annotation { "Feature Type Name" : "Feature", "Feature Type Description" : "" }
export const myFeature = defineFeature(function(context is Context, id is Id, definition is map)
    precondition{}
    {
        {
            var Q0;
            Q0=qCreatedBy(makeId("Top.planeOp"),FACE);
            var sketch = newSketch(context, id + "F0", { "sketchPlane" : qUnion([Q0])});
            skLineSegment(sketch, "E0.bottom", {"start": v(38, -38) * mm, "end": v(-38, -38) * mm});
            skLineSegment(sketch, "E0.top", {"start": v(38, 38) * mm, "end": v(-38, 38) * mm});
            skLineSegment(sketch, "E0.left", {"start": v(38, -38) * mm, "end": v(38, 38) * mm});
            skLineSegment(sketch, "E0.right", {"start": v(-38, -38) * mm, "end": v(-38, 38) * mm});
            skPoint(sketch, "E0.middle", {"position": v(0, 0) * mm});
            skLineSegment(sketch, "E1.0", {"start": v(-35, -35) * mm, "end": v(-35, 35) * mm});
            skLineSegment(sketch, "E1.1", {"start": v(35, -35) * mm, "end": v(-35, -35) * mm});
            skLineSegment(sketch, "E1.2", {"start": v(35, -35) * mm, "end": v(35, 35) * mm});
            skLineSegment(sketch, "E1.3", {"start": v(35, 35) * mm, "end": v(-35, 35) * mm});
            skSolve(sketch);
        }
        {
            var Q0;
            Q0=makeQuery(id+"F0.imprint","IMPRINT",FACE,{"disambiguationData":[TD([[makeQuery(id+"F0.imprint","IMPRINT",EDGE,{"derivedFrom":sQuery(id+"F0.wireOp",EDGE,"E0.bottom")}),-1.0]])]});
            extrude(context, id + "F1", {"entities" : qUnion([Q0]), "depth" : 122 * mm, "offsetDistance" : 25 * mm});
        }
        {
            var Q0;
            Q0=makeQuery(id+"F0.imprint","IMPRINT",FACE,{"disambiguationData":[TD([[makeQuery(id+"F0.imprint","IMPRINT",EDGE,{"derivedFrom":sQuery(id+"F0.wireOp",EDGE,"E0.bottom")}),-1.0]])]});
            var Q1;
            Q1=makeQuery(id+"F0.imprint","IMPRINT",FACE,{"disambiguationData":[TD([[makeQuery(id+"F0.imprint","IMPRINT",EDGE,{"derivedFrom":sQuery(id+"F0.wireOp",EDGE,"E1.0")}),-1.0]])]});
            extrude(context, id + "F2", {"entities" : qUnion([Q0, Q1]), "operationType" : NewBodyOperationType.ADD, "oppositeDirection" : true, "depth" : 3 * mm, "offsetDistance" : 25 * mm});
        }
        {
            var Q0;
            {var subQ0=sQuery(id+"F0.wireOp",EDGE,"E0.top");Q0=makeQuery(id+"F2.boolean.opBoolean","MERGE",FACE,{"derivedFrom":[makeQuery(id+"F1.opExtrude","SWEPT_FACE",FACE,{"disambiguationData":[OSD([subQ0])]}),makeQuery(id+"F2.opExtrude","SWEPT_FACE",FACE,{"disambiguationData":[OSD([subQ0])]})]});}
            var sketch = newSketch(context, id + "F3", { "sketchPlane" : qUnion([Q0])});
            skCircle(sketch, "E2", {"center": v(-23.93, 112.63) * mm, "radius": 5.45 * mm});
            skCircle(sketch, "E3", {"center": v(-14.07, 99.88) * mm, "radius": 7.74 * mm});
            skCircle(sketch, "E4", {"center": v(-18.4, 76.32) * mm, "radius": 12.07 * mm});
            skCircle(sketch, "E5", {"center": v(8.3, 72.71) * mm, "radius": 9.52 * mm});
            skCircle(sketch, "E6", {"center": v(12.62, 91.47) * mm, "radius": 4.62 * mm});
            skCircle(sketch, "E7", {"center": v(0, 45.06) * mm, "radius": 3.83 * mm});
            skCircle(sketch, "E8", {"center": v(-13.35, 35.44) * mm, "radius": 5.61 * mm});
            skCircle(sketch, "E9", {"center": v(7.1, 18.6) * mm, "radius": 4.64 * mm});
            skCircle(sketch, "E10", {"center": v(17.43, 39.05) * mm, "radius": 6.47 * mm});
            skCircle(sketch, "E11", {"center": v(26.57, 57.56) * mm, "radius": 7.49 * mm});
            skCircle(sketch, "E12", {"center": v(8.78, 110.95) * mm, "radius": 4.28 * mm});
            skCircle(sketch, "E13", {"center": v(23.2, 107.1) * mm, "radius": 5.3 * mm});
            skCircle(sketch, "E14", {"center": v(-19.36, 53.71) * mm, "radius": 8 * mm});
            skCircle(sketch, "E15", {"center": v(-20.56, 18.85) * mm, "radius": 4.47 * mm});
            skCircle(sketch, "E16", {"center": v(-8.78, 9.23) * mm, "radius": 6.54 * mm});
            skCircle(sketch, "E17", {"center": v(22.96, 16.68) * mm, "radius": 3.91 * mm});
            skCircle(sketch, "E18", {"center": v(26.57, 7.06) * mm, "radius": 2.56 * mm});
            skCircle(sketch, "E19", {"center": v(9.74, 7.79) * mm, "radius": 3.68 * mm});
            skCircle(sketch, "E20", {"center": v(-28.98, 8.75) * mm, "radius": 4.34 * mm});
            skSolve(sketch);
        }
        {
            var Q0;
            Q0 = qSketchRegion(id + "F3", true);
            extrude(context, id + "F4", {"entities" : qUnion([Q0]), "oppositeDirection" : true, "depth" : 5 * mm, "offsetDistance" : 25 * mm});
        }
        {
            var Q0;
            Q0=qCreatedBy(makeId("Front.planeOp"),FACE);
            var sketch = newSketch(context, id + "F5", { "sketchPlane" : qUnion([Q0])});
            skLineSegment(sketch, "E21", {"start": v(0, 24.74) * mm, "end": v(0, 105.67) * mm, "construction": true});
            skSolve(sketch);
        }
        {
            var Q0;
            Q0=makeQuery(id+"F4.opExtrude","SWEPT_BODY",BODY,{"disambiguationData":[OSD([sQuery(id+"F3.wireOp",EDGE,"E2")])]});
            var Q1;
            Q1=makeQuery(id+"F4.opExtrude","SWEPT_BODY",BODY,{"disambiguationData":[OSD([sQuery(id+"F3.wireOp",EDGE,"E3")])]});
            var Q2;
            Q2=makeQuery(id+"F4.opExtrude","SWEPT_BODY",BODY,{"disambiguationData":[OSD([sQuery(id+"F3.wireOp",EDGE,"E4")])]});
            var Q3;
            Q3=makeQuery(id+"F4.opExtrude","SWEPT_BODY",BODY,{"disambiguationData":[OSD([sQuery(id+"F3.wireOp",EDGE,"E5")])]});
            var Q4;
            Q4=makeQuery(id+"F4.opExtrude","SWEPT_BODY",BODY,{"disambiguationData":[OSD([sQuery(id+"F3.wireOp",EDGE,"E6")])]});
            var Q5;
            Q5=makeQuery(id+"F4.opExtrude","SWEPT_BODY",BODY,{"disambiguationData":[OSD([sQuery(id+"F3.wireOp",EDGE,"E7")])]});
            var Q6;
            Q6=makeQuery(id+"F4.opExtrude","SWEPT_BODY",BODY,{"disambiguationData":[OSD([sQuery(id+"F3.wireOp",EDGE,"E8")])]});
            var Q7;
            Q7=makeQuery(id+"F4.opExtrude","SWEPT_BODY",BODY,{"disambiguationData":[OSD([sQuery(id+"F3.wireOp",EDGE,"E9")])]});
            var Q8;
            Q8=makeQuery(id+"F4.opExtrude","SWEPT_BODY",BODY,{"disambiguationData":[OSD([sQuery(id+"F3.wireOp",EDGE,"E10")])]});
            var Q9;
            Q9=makeQuery(id+"F4.opExtrude","SWEPT_BODY",BODY,{"disambiguationData":[OSD([sQuery(id+"F3.wireOp",EDGE,"E11")])]});
            var Q10;
            Q10=makeQuery(id+"F4.opExtrude","SWEPT_BODY",BODY,{"disambiguationData":[OSD([sQuery(id+"F3.wireOp",EDGE,"E12")])]});
            var Q11;
            Q11=makeQuery(id+"F4.opExtrude","SWEPT_BODY",BODY,{"disambiguationData":[OSD([sQuery(id+"F3.wireOp",EDGE,"E13")])]});
            var Q12;
            Q12=makeQuery(id+"F4.opExtrude","SWEPT_BODY",BODY,{"disambiguationData":[OSD([sQuery(id+"F3.wireOp",EDGE,"E14")])]});
            var Q13;
            Q13=makeQuery(id+"F4.opExtrude","SWEPT_BODY",BODY,{"disambiguationData":[OSD([sQuery(id+"F3.wireOp",EDGE,"E15")])]});
            var Q14;
            Q14=makeQuery(id+"F4.opExtrude","SWEPT_BODY",BODY,{"disambiguationData":[OSD([sQuery(id+"F3.wireOp",EDGE,"E16")])]});
            var Q15;
            Q15=makeQuery(id+"F4.opExtrude","SWEPT_BODY",BODY,{"disambiguationData":[OSD([sQuery(id+"F3.wireOp",EDGE,"E17")])]});
            var Q16;
            Q16=makeQuery(id+"F4.opExtrude","SWEPT_BODY",BODY,{"disambiguationData":[OSD([sQuery(id+"F3.wireOp",EDGE,"E18")])]});
            var Q17;
            Q17=makeQuery(id+"F4.opExtrude","SWEPT_BODY",BODY,{"disambiguationData":[OSD([sQuery(id+"F3.wireOp",EDGE,"E19")])]});
            var Q18;
            Q18=makeQuery(id+"F4.opExtrude","SWEPT_BODY",BODY,{"disambiguationData":[OSD([sQuery(id+"F3.wireOp",EDGE,"E20")])]});
            var Q19;
            Q19=sQuery(id+"F5.wireOp",EDGE,"E21");
            circularPattern(context, id + "F6", {"entities" : qUnion([Q0, Q1, Q2, Q3, Q4, Q5, Q6, Q7, Q8, Q9, Q10, Q11, Q12, Q13, Q14, Q15, Q16, Q17, Q18]), "axis" : qUnion([Q19]), "angle" : 360 * degree, "instanceCount" : 4, "equalSpace" : true});
        }
        {
            var Q0;
            Q0=makeQuery(id+"F4.opExtrude","SWEPT_BODY",BODY,{"disambiguationData":[OSD([sQuery(id+"F3.wireOp",EDGE,"E2")])]});
            var Q1;
            Q1=makeQuery(id+"F4.opExtrude","SWEPT_BODY",BODY,{"disambiguationData":[OSD([sQuery(id+"F3.wireOp",EDGE,"E3")])]});
            var Q2;
            Q2=makeQuery(id+"F4.opExtrude","SWEPT_BODY",BODY,{"disambiguationData":[OSD([sQuery(id+"F3.wireOp",EDGE,"E4")])]});
            var Q3;
            Q3=makeQuery(id+"F4.opExtrude","SWEPT_BODY",BODY,{"disambiguationData":[OSD([sQuery(id+"F3.wireOp",EDGE,"E5")])]});
            var Q4;
            Q4=makeQuery(id+"F4.opExtrude","SWEPT_BODY",BODY,{"disambiguationData":[OSD([sQuery(id+"F3.wireOp",EDGE,"E6")])]});
            var Q5;
            Q5=makeQuery(id+"F4.opExtrude","SWEPT_BODY",BODY,{"disambiguationData":[OSD([sQuery(id+"F3.wireOp",EDGE,"E7")])]});
            var Q6;
            Q6=makeQuery(id+"F4.opExtrude","SWEPT_BODY",BODY,{"disambiguationData":[OSD([sQuery(id+"F3.wireOp",EDGE,"E8")])]});
            var Q7;
            Q7=makeQuery(id+"F4.opExtrude","SWEPT_BODY",BODY,{"disambiguationData":[OSD([sQuery(id+"F3.wireOp",EDGE,"E9")])]});
            var Q8;
            Q8=makeQuery(id+"F4.opExtrude","SWEPT_BODY",BODY,{"disambiguationData":[OSD([sQuery(id+"F3.wireOp",EDGE,"E10")])]});
            var Q9;
            Q9=makeQuery(id+"F4.opExtrude","SWEPT_BODY",BODY,{"disambiguationData":[OSD([sQuery(id+"F3.wireOp",EDGE,"E11")])]});
            var Q10;
            Q10=makeQuery(id+"F4.opExtrude","SWEPT_BODY",BODY,{"disambiguationData":[OSD([sQuery(id+"F3.wireOp",EDGE,"E12")])]});
            var Q11;
            Q11=makeQuery(id+"F4.opExtrude","SWEPT_BODY",BODY,{"disambiguationData":[OSD([sQuery(id+"F3.wireOp",EDGE,"E13")])]});
            var Q12;
            Q12=makeQuery(id+"F4.opExtrude","SWEPT_BODY",BODY,{"disambiguationData":[OSD([sQuery(id+"F3.wireOp",EDGE,"E14")])]});
            var Q13;
            Q13=makeQuery(id+"F4.opExtrude","SWEPT_BODY",BODY,{"disambiguationData":[OSD([sQuery(id+"F3.wireOp",EDGE,"E15")])]});
            var Q14;
            Q14=makeQuery(id+"F4.opExtrude","SWEPT_BODY",BODY,{"disambiguationData":[OSD([sQuery(id+"F3.wireOp",EDGE,"E16")])]});
            var Q15;
            Q15=makeQuery(id+"F4.opExtrude","SWEPT_BODY",BODY,{"disambiguationData":[OSD([sQuery(id+"F3.wireOp",EDGE,"E17")])]});
            var Q16;
            Q16=makeQuery(id+"F4.opExtrude","SWEPT_BODY",BODY,{"disambiguationData":[OSD([sQuery(id+"F3.wireOp",EDGE,"E18")])]});
            var Q17;
            Q17=makeQuery(id+"F4.opExtrude","SWEPT_BODY",BODY,{"disambiguationData":[OSD([sQuery(id+"F3.wireOp",EDGE,"E19")])]});
            var Q18;
            Q18=makeQuery(id+"F4.opExtrude","SWEPT_BODY",BODY,{"disambiguationData":[OSD([sQuery(id+"F3.wireOp",EDGE,"E20")])]});
            var Q19;
            Q19=makeQuery(id+"F6.opPattern","COPY",BODY,{"derivedFrom":makeQuery(id+"F4.opExtrude","SWEPT_BODY",BODY,{"disambiguationData":[OSD([sQuery(id+"F3.wireOp",EDGE,"E2")])]}),"instanceName":"1"});
            var Q20;
            Q20=makeQuery(id+"F6.opPattern","COPY",BODY,{"derivedFrom":makeQuery(id+"F4.opExtrude","SWEPT_BODY",BODY,{"disambiguationData":[OSD([sQuery(id+"F3.wireOp",EDGE,"E3")])]}),"instanceName":"1"});
            var Q21;
            Q21=makeQuery(id+"F6.opPattern","COPY",BODY,{"derivedFrom":makeQuery(id+"F4.opExtrude","SWEPT_BODY",BODY,{"disambiguationData":[OSD([sQuery(id+"F3.wireOp",EDGE,"E4")])]}),"instanceName":"1"});
            var Q22;
            Q22=makeQuery(id+"F6.opPattern","COPY",BODY,{"derivedFrom":makeQuery(id+"F4.opExtrude","SWEPT_BODY",BODY,{"disambiguationData":[OSD([sQuery(id+"F3.wireOp",EDGE,"E5")])]}),"instanceName":"1"});
            var Q23;
            Q23=makeQuery(id+"F6.opPattern","COPY",BODY,{"derivedFrom":makeQuery(id+"F4.opExtrude","SWEPT_BODY",BODY,{"disambiguationData":[OSD([sQuery(id+"F3.wireOp",EDGE,"E6")])]}),"instanceName":"1"});
            var Q24;
            Q24=makeQuery(id+"F6.opPattern","COPY",BODY,{"derivedFrom":makeQuery(id+"F4.opExtrude","SWEPT_BODY",BODY,{"disambiguationData":[OSD([sQuery(id+"F3.wireOp",EDGE,"E7")])]}),"instanceName":"1"});
            var Q25;
            Q25=makeQuery(id+"F6.opPattern","COPY",BODY,{"derivedFrom":makeQuery(id+"F4.opExtrude","SWEPT_BODY",BODY,{"disambiguationData":[OSD([sQuery(id+"F3.wireOp",EDGE,"E8")])]}),"instanceName":"1"});
            var Q26;
            Q26=makeQuery(id+"F6.opPattern","COPY",BODY,{"derivedFrom":makeQuery(id+"F4.opExtrude","SWEPT_BODY",BODY,{"disambiguationData":[OSD([sQuery(id+"F3.wireOp",EDGE,"E9")])]}),"instanceName":"1"});
            var Q27;
            Q27=makeQuery(id+"F6.opPattern","COPY",BODY,{"derivedFrom":makeQuery(id+"F4.opExtrude","SWEPT_BODY",BODY,{"disambiguationData":[OSD([sQuery(id+"F3.wireOp",EDGE,"E10")])]}),"instanceName":"1"});
            var Q28;
            Q28=makeQuery(id+"F6.opPattern","COPY",BODY,{"derivedFrom":makeQuery(id+"F4.opExtrude","SWEPT_BODY",BODY,{"disambiguationData":[OSD([sQuery(id+"F3.wireOp",EDGE,"E11")])]}),"instanceName":"1"});
            var Q29;
            Q29=makeQuery(id+"F6.opPattern","COPY",BODY,{"derivedFrom":makeQuery(id+"F4.opExtrude","SWEPT_BODY",BODY,{"disambiguationData":[OSD([sQuery(id+"F3.wireOp",EDGE,"E12")])]}),"instanceName":"1"});
            var Q30;
            Q30=makeQuery(id+"F6.opPattern","COPY",BODY,{"derivedFrom":makeQuery(id+"F4.opExtrude","SWEPT_BODY",BODY,{"disambiguationData":[OSD([sQuery(id+"F3.wireOp",EDGE,"E13")])]}),"instanceName":"1"});
            var Q31;
            Q31=makeQuery(id+"F6.opPattern","COPY",BODY,{"derivedFrom":makeQuery(id+"F4.opExtrude","SWEPT_BODY",BODY,{"disambiguationData":[OSD([sQuery(id+"F3.wireOp",EDGE,"E14")])]}),"instanceName":"1"});
            var Q32;
            Q32=makeQuery(id+"F6.opPattern","COPY",BODY,{"derivedFrom":makeQuery(id+"F4.opExtrude","SWEPT_BODY",BODY,{"disambiguationData":[OSD([sQuery(id+"F3.wireOp",EDGE,"E15")])]}),"instanceName":"1"});
            var Q33;
            Q33=makeQuery(id+"F6.opPattern","COPY",BODY,{"derivedFrom":makeQuery(id+"F4.opExtrude","SWEPT_BODY",BODY,{"disambiguationData":[OSD([sQuery(id+"F3.wireOp",EDGE,"E16")])]}),"instanceName":"1"});
            var Q34;
            Q34=makeQuery(id+"F6.opPattern","COPY",BODY,{"derivedFrom":makeQuery(id+"F4.opExtrude","SWEPT_BODY",BODY,{"disambiguationData":[OSD([sQuery(id+"F3.wireOp",EDGE,"E17")])]}),"instanceName":"1"});
            var Q35;
            Q35=makeQuery(id+"F6.opPattern","COPY",BODY,{"derivedFrom":makeQuery(id+"F4.opExtrude","SWEPT_BODY",BODY,{"disambiguationData":[OSD([sQuery(id+"F3.wireOp",EDGE,"E18")])]}),"instanceName":"1"});
            var Q36;
            Q36=makeQuery(id+"F6.opPattern","COPY",BODY,{"derivedFrom":makeQuery(id+"F4.opExtrude","SWEPT_BODY",BODY,{"disambiguationData":[OSD([sQuery(id+"F3.wireOp",EDGE,"E19")])]}),"instanceName":"1"});
            var Q37;
            Q37=makeQuery(id+"F6.opPattern","COPY",BODY,{"derivedFrom":makeQuery(id+"F4.opExtrude","SWEPT_BODY",BODY,{"disambiguationData":[OSD([sQuery(id+"F3.wireOp",EDGE,"E20")])]}),"instanceName":"1"});
            var Q38;
            Q38=makeQuery(id+"F6.opPattern","COPY",BODY,{"derivedFrom":makeQuery(id+"F4.opExtrude","SWEPT_BODY",BODY,{"disambiguationData":[OSD([sQuery(id+"F3.wireOp",EDGE,"E2")])]}),"instanceName":"2"});
            var Q39;
            Q39=makeQuery(id+"F6.opPattern","COPY",BODY,{"derivedFrom":makeQuery(id+"F4.opExtrude","SWEPT_BODY",BODY,{"disambiguationData":[OSD([sQuery(id+"F3.wireOp",EDGE,"E3")])]}),"instanceName":"2"});
            var Q40;
            Q40=makeQuery(id+"F6.opPattern","COPY",BODY,{"derivedFrom":makeQuery(id+"F4.opExtrude","SWEPT_BODY",BODY,{"disambiguationData":[OSD([sQuery(id+"F3.wireOp",EDGE,"E4")])]}),"instanceName":"2"});
            var Q41;
            Q41=makeQuery(id+"F6.opPattern","COPY",BODY,{"derivedFrom":makeQuery(id+"F4.opExtrude","SWEPT_BODY",BODY,{"disambiguationData":[OSD([sQuery(id+"F3.wireOp",EDGE,"E5")])]}),"instanceName":"2"});
            var Q42;
            Q42=makeQuery(id+"F6.opPattern","COPY",BODY,{"derivedFrom":makeQuery(id+"F4.opExtrude","SWEPT_BODY",BODY,{"disambiguationData":[OSD([sQuery(id+"F3.wireOp",EDGE,"E6")])]}),"instanceName":"2"});
            var Q43;
            Q43=makeQuery(id+"F6.opPattern","COPY",BODY,{"derivedFrom":makeQuery(id+"F4.opExtrude","SWEPT_BODY",BODY,{"disambiguationData":[OSD([sQuery(id+"F3.wireOp",EDGE,"E7")])]}),"instanceName":"2"});
            var Q44;
            Q44=makeQuery(id+"F6.opPattern","COPY",BODY,{"derivedFrom":makeQuery(id+"F4.opExtrude","SWEPT_BODY",BODY,{"disambiguationData":[OSD([sQuery(id+"F3.wireOp",EDGE,"E8")])]}),"instanceName":"2"});
            var Q45;
            Q45=makeQuery(id+"F6.opPattern","COPY",BODY,{"derivedFrom":makeQuery(id+"F4.opExtrude","SWEPT_BODY",BODY,{"disambiguationData":[OSD([sQuery(id+"F3.wireOp",EDGE,"E9")])]}),"instanceName":"2"});
            var Q46;
            Q46=makeQuery(id+"F6.opPattern","COPY",BODY,{"derivedFrom":makeQuery(id+"F4.opExtrude","SWEPT_BODY",BODY,{"disambiguationData":[OSD([sQuery(id+"F3.wireOp",EDGE,"E10")])]}),"instanceName":"2"});
            var Q47;
            Q47=makeQuery(id+"F6.opPattern","COPY",BODY,{"derivedFrom":makeQuery(id+"F4.opExtrude","SWEPT_BODY",BODY,{"disambiguationData":[OSD([sQuery(id+"F3.wireOp",EDGE,"E11")])]}),"instanceName":"2"});
            var Q48;
            Q48=makeQuery(id+"F6.opPattern","COPY",BODY,{"derivedFrom":makeQuery(id+"F4.opExtrude","SWEPT_BODY",BODY,{"disambiguationData":[OSD([sQuery(id+"F3.wireOp",EDGE,"E12")])]}),"instanceName":"2"});
            var Q49;
            Q49=makeQuery(id+"F6.opPattern","COPY",BODY,{"derivedFrom":makeQuery(id+"F4.opExtrude","SWEPT_BODY",BODY,{"disambiguationData":[OSD([sQuery(id+"F3.wireOp",EDGE,"E13")])]}),"instanceName":"2"});
            var Q50;
            Q50=makeQuery(id+"F6.opPattern","COPY",BODY,{"derivedFrom":makeQuery(id+"F4.opExtrude","SWEPT_BODY",BODY,{"disambiguationData":[OSD([sQuery(id+"F3.wireOp",EDGE,"E14")])]}),"instanceName":"2"});
            var Q51;
            Q51=makeQuery(id+"F6.opPattern","COPY",BODY,{"derivedFrom":makeQuery(id+"F4.opExtrude","SWEPT_BODY",BODY,{"disambiguationData":[OSD([sQuery(id+"F3.wireOp",EDGE,"E15")])]}),"instanceName":"2"});
            var Q52;
            Q52=makeQuery(id+"F6.opPattern","COPY",BODY,{"derivedFrom":makeQuery(id+"F4.opExtrude","SWEPT_BODY",BODY,{"disambiguationData":[OSD([sQuery(id+"F3.wireOp",EDGE,"E16")])]}),"instanceName":"2"});
            var Q53;
            Q53=makeQuery(id+"F6.opPattern","COPY",BODY,{"derivedFrom":makeQuery(id+"F4.opExtrude","SWEPT_BODY",BODY,{"disambiguationData":[OSD([sQuery(id+"F3.wireOp",EDGE,"E17")])]}),"instanceName":"2"});
            var Q54;
            Q54=makeQuery(id+"F6.opPattern","COPY",BODY,{"derivedFrom":makeQuery(id+"F4.opExtrude","SWEPT_BODY",BODY,{"disambiguationData":[OSD([sQuery(id+"F3.wireOp",EDGE,"E18")])]}),"instanceName":"2"});
            var Q55;
            Q55=makeQuery(id+"F6.opPattern","COPY",BODY,{"derivedFrom":makeQuery(id+"F4.opExtrude","SWEPT_BODY",BODY,{"disambiguationData":[OSD([sQuery(id+"F3.wireOp",EDGE,"E19")])]}),"instanceName":"2"});
            var Q56;
            Q56=makeQuery(id+"F6.opPattern","COPY",BODY,{"derivedFrom":makeQuery(id+"F4.opExtrude","SWEPT_BODY",BODY,{"disambiguationData":[OSD([sQuery(id+"F3.wireOp",EDGE,"E20")])]}),"instanceName":"2"});
            var Q57;
            Q57=makeQuery(id+"F6.opPattern","COPY",BODY,{"derivedFrom":makeQuery(id+"F4.opExtrude","SWEPT_BODY",BODY,{"disambiguationData":[OSD([sQuery(id+"F3.wireOp",EDGE,"E2")])]}),"instanceName":"3"});
            var Q58;
            Q58=makeQuery(id+"F6.opPattern","COPY",BODY,{"derivedFrom":makeQuery(id+"F4.opExtrude","SWEPT_BODY",BODY,{"disambiguationData":[OSD([sQuery(id+"F3.wireOp",EDGE,"E3")])]}),"instanceName":"3"});
            var Q59;
            Q59=makeQuery(id+"F6.opPattern","COPY",BODY,{"derivedFrom":makeQuery(id+"F4.opExtrude","SWEPT_BODY",BODY,{"disambiguationData":[OSD([sQuery(id+"F3.wireOp",EDGE,"E4")])]}),"instanceName":"3"});
            var Q60;
            Q60=makeQuery(id+"F6.opPattern","COPY",BODY,{"derivedFrom":makeQuery(id+"F4.opExtrude","SWEPT_BODY",BODY,{"disambiguationData":[OSD([sQuery(id+"F3.wireOp",EDGE,"E5")])]}),"instanceName":"3"});
            var Q61;
            Q61=makeQuery(id+"F6.opPattern","COPY",BODY,{"derivedFrom":makeQuery(id+"F4.opExtrude","SWEPT_BODY",BODY,{"disambiguationData":[OSD([sQuery(id+"F3.wireOp",EDGE,"E6")])]}),"instanceName":"3"});
            var Q62;
            Q62=makeQuery(id+"F6.opPattern","COPY",BODY,{"derivedFrom":makeQuery(id+"F4.opExtrude","SWEPT_BODY",BODY,{"disambiguationData":[OSD([sQuery(id+"F3.wireOp",EDGE,"E7")])]}),"instanceName":"3"});
            var Q63;
            Q63=makeQuery(id+"F6.opPattern","COPY",BODY,{"derivedFrom":makeQuery(id+"F4.opExtrude","SWEPT_BODY",BODY,{"disambiguationData":[OSD([sQuery(id+"F3.wireOp",EDGE,"E8")])]}),"instanceName":"3"});
            var Q64;
            Q64=makeQuery(id+"F6.opPattern","COPY",BODY,{"derivedFrom":makeQuery(id+"F4.opExtrude","SWEPT_BODY",BODY,{"disambiguationData":[OSD([sQuery(id+"F3.wireOp",EDGE,"E9")])]}),"instanceName":"3"});
            var Q65;
            Q65=makeQuery(id+"F6.opPattern","COPY",BODY,{"derivedFrom":makeQuery(id+"F4.opExtrude","SWEPT_BODY",BODY,{"disambiguationData":[OSD([sQuery(id+"F3.wireOp",EDGE,"E10")])]}),"instanceName":"3"});
            var Q66;
            Q66=makeQuery(id+"F6.opPattern","COPY",BODY,{"derivedFrom":makeQuery(id+"F4.opExtrude","SWEPT_BODY",BODY,{"disambiguationData":[OSD([sQuery(id+"F3.wireOp",EDGE,"E11")])]}),"instanceName":"3"});
            var Q67;
            Q67=makeQuery(id+"F6.opPattern","COPY",BODY,{"derivedFrom":makeQuery(id+"F4.opExtrude","SWEPT_BODY",BODY,{"disambiguationData":[OSD([sQuery(id+"F3.wireOp",EDGE,"E12")])]}),"instanceName":"3"});
            var Q68;
            Q68=makeQuery(id+"F6.opPattern","COPY",BODY,{"derivedFrom":makeQuery(id+"F4.opExtrude","SWEPT_BODY",BODY,{"disambiguationData":[OSD([sQuery(id+"F3.wireOp",EDGE,"E13")])]}),"instanceName":"3"});
            var Q69;
            Q69=makeQuery(id+"F6.opPattern","COPY",BODY,{"derivedFrom":makeQuery(id+"F4.opExtrude","SWEPT_BODY",BODY,{"disambiguationData":[OSD([sQuery(id+"F3.wireOp",EDGE,"E14")])]}),"instanceName":"3"});
            var Q70;
            Q70=makeQuery(id+"F6.opPattern","COPY",BODY,{"derivedFrom":makeQuery(id+"F4.opExtrude","SWEPT_BODY",BODY,{"disambiguationData":[OSD([sQuery(id+"F3.wireOp",EDGE,"E15")])]}),"instanceName":"3"});
            var Q71;
            Q71=makeQuery(id+"F6.opPattern","COPY",BODY,{"derivedFrom":makeQuery(id+"F4.opExtrude","SWEPT_BODY",BODY,{"disambiguationData":[OSD([sQuery(id+"F3.wireOp",EDGE,"E16")])]}),"instanceName":"3"});
            var Q72;
            Q72=makeQuery(id+"F6.opPattern","COPY",BODY,{"derivedFrom":makeQuery(id+"F4.opExtrude","SWEPT_BODY",BODY,{"disambiguationData":[OSD([sQuery(id+"F3.wireOp",EDGE,"E17")])]}),"instanceName":"3"});
            var Q73;
            Q73=makeQuery(id+"F6.opPattern","COPY",BODY,{"derivedFrom":makeQuery(id+"F4.opExtrude","SWEPT_BODY",BODY,{"disambiguationData":[OSD([sQuery(id+"F3.wireOp",EDGE,"E18")])]}),"instanceName":"3"});
            var Q74;
            Q74=makeQuery(id+"F6.opPattern","COPY",BODY,{"derivedFrom":makeQuery(id+"F4.opExtrude","SWEPT_BODY",BODY,{"disambiguationData":[OSD([sQuery(id+"F3.wireOp",EDGE,"E19")])]}),"instanceName":"3"});
            var Q75;
            Q75=makeQuery(id+"F6.opPattern","COPY",BODY,{"derivedFrom":makeQuery(id+"F4.opExtrude","SWEPT_BODY",BODY,{"disambiguationData":[OSD([sQuery(id+"F3.wireOp",EDGE,"E20")])]}),"instanceName":"3"});
            var Q76;
            Q76=makeQuery(id+"F1.opExtrude","SWEPT_BODY",BODY,{"disambiguationData":[OSD([sQuery(id+"F0.wireOp",EDGE,"E0.bottom"),sQuery(id+"F0.wireOp",EDGE,"E0.top"),sQuery(id+"F0.wireOp",EDGE,"E0.left"),sQuery(id+"F0.wireOp",EDGE,"E0.right"),sQuery(id+"F0.wireOp",EDGE,"E1.0"),sQuery(id+"F0.wireOp",EDGE,"E1.1"),sQuery(id+"F0.wireOp",EDGE,"E1.2"),sQuery(id+"F0.wireOp",EDGE,"E1.3")])]});
            booleanBodies(context, id + "F7", {"operationType" : BooleanOperationType.SUBTRACTION, "tools" : qUnion([Q0, Q1, Q2, Q3, Q4, Q5, Q6, Q7, Q8, Q9, Q10, Q11, Q12, Q13, Q14, Q15, Q16, Q17, Q18, Q19, Q20, Q21, Q22, Q23, Q24, Q25, Q26, Q27, Q28, Q29, Q30, Q31, Q32, Q33, Q34, Q35, Q36, Q37, Q38, Q39, Q40, Q41, Q42, Q43, Q44, Q45, Q46, Q47, Q48, Q49, Q50, Q51, Q52, Q53, Q54, Q55, Q56, Q57, Q58, Q59, Q60, Q61, Q62, Q63, Q64, Q65, Q66, Q67, Q68, Q69, Q70, Q71, Q72, Q73, Q74, Q75]), "targets" : qUnion([Q76])});
        }
        {
            var Q0;
            {var subQ0=sQuery(id+"F0.wireOp",EDGE,"E0.left");var subQ1=sQuery(id+"F0.wireOp",EDGE,"E0.bottom");Q0=makeQuery(id+"F2.boolean.opBoolean","MERGE",EDGE,{"derivedFrom":[makeQuery(id+"F1.opExtrude","SWEPT_EDGE",EDGE,{"disambiguationData":[OSD([subQ1,subQ0])]}),makeQuery(id+"F2.opExtrude","SWEPT_EDGE",EDGE,{"disambiguationData":[OSD([subQ1,subQ0])]})]});}
            var Q1;
            {var subQ0=sQuery(id+"F0.wireOp",EDGE,"E0.left");var subQ1=sQuery(id+"F0.wireOp",EDGE,"E0.top");Q1=makeQuery(id+"F2.boolean.opBoolean","MERGE",EDGE,{"derivedFrom":[makeQuery(id+"F1.opExtrude","SWEPT_EDGE",EDGE,{"disambiguationData":[OSD([subQ1,subQ0])]}),makeQuery(id+"F2.opExtrude","SWEPT_EDGE",EDGE,{"disambiguationData":[OSD([subQ1,subQ0])]})]});}
            var Q2;
            {var subQ0=sQuery(id+"F0.wireOp",EDGE,"E0.right");var subQ1=sQuery(id+"F0.wireOp",EDGE,"E0.top");Q2=makeQuery(id+"F2.boolean.opBoolean","MERGE",EDGE,{"derivedFrom":[makeQuery(id+"F1.opExtrude","SWEPT_EDGE",EDGE,{"disambiguationData":[OSD([subQ1,subQ0])]}),makeQuery(id+"F2.opExtrude","SWEPT_EDGE",EDGE,{"disambiguationData":[OSD([subQ1,subQ0])]})]});}
            var Q3;
            {var subQ0=sQuery(id+"F0.wireOp",EDGE,"E0.right");var subQ1=sQuery(id+"F0.wireOp",EDGE,"E0.bottom");Q3=makeQuery(id+"F2.boolean.opBoolean","MERGE",EDGE,{"derivedFrom":[makeQuery(id+"F1.opExtrude","SWEPT_EDGE",EDGE,{"disambiguationData":[OSD([subQ1,subQ0])]}),makeQuery(id+"F2.opExtrude","SWEPT_EDGE",EDGE,{"disambiguationData":[OSD([subQ1,subQ0])]})]});}
            var Q4;
            Q4=makeQuery(id+"F1.opExtrude","SWEPT_EDGE",EDGE,{"disambiguationData":[OSD([sQuery(id+"F0.wireOp",EDGE,"E1.0"),sQuery(id+"F0.wireOp",EDGE,"E1.1")])]});
            var Q5;
            Q5=makeQuery(id+"F1.opExtrude","SWEPT_EDGE",EDGE,{"disambiguationData":[OSD([sQuery(id+"F0.wireOp",EDGE,"E1.1"),sQuery(id+"F0.wireOp",EDGE,"E1.2")])]});
            var Q6;
            Q6=makeQuery(id+"F1.opExtrude","SWEPT_EDGE",EDGE,{"disambiguationData":[OSD([sQuery(id+"F0.wireOp",EDGE,"E1.2"),sQuery(id+"F0.wireOp",EDGE,"E1.3")])]});
            var Q7;
            Q7=makeQuery(id+"F1.opExtrude","SWEPT_EDGE",EDGE,{"disambiguationData":[OSD([sQuery(id+"F0.wireOp",EDGE,"E1.0"),sQuery(id+"F0.wireOp",EDGE,"E1.3")])]});
            fillet(context, id + "F8", {"entities" : qUnion([Q0, Q1, Q2, Q3, Q4, Q5, Q6, Q7]), "radius" : 5 * mm, "tangentPropagation" : true, "allowEdgeOverflow" : false});
        }
        {
            var Q0;
            Q0=makeQuery(id+"F1.opExtrude","CAP_FACE",FACE,{"disambiguationData":[OSD([sQuery(id+"F0.wireOp",EDGE,"E0.bottom"),sQuery(id+"F0.wireOp",EDGE,"E0.top"),sQuery(id+"F0.wireOp",EDGE,"E0.left"),sQuery(id+"F0.wireOp",EDGE,"E0.right"),sQuery(id+"F0.wireOp",EDGE,"E1.0"),sQuery(id+"F0.wireOp",EDGE,"E1.1"),sQuery(id+"F0.wireOp",EDGE,"E1.2"),sQuery(id+"F0.wireOp",EDGE,"E1.3")])],"isStart":false});
            fillet(context, id + "F9", {"entities" : qUnion([Q0]), "radius" : 1 * mm, "tangentPropagation" : true, "allowEdgeOverflow" : false});
        }
        {
            var Q0;
            Q0=makeQuery(id+"F2.opExtrude","CAP_FACE",FACE,{"disambiguationData":[OSD([sQuery(id+"F0.wireOp",EDGE,"E0.bottom"),sQuery(id+"F0.wireOp",EDGE,"E0.top"),sQuery(id+"F0.wireOp",EDGE,"E0.left"),sQuery(id+"F0.wireOp",EDGE,"E0.right")])],"isStart":false});
            var sketch = newSketch(context, id + "F10", { "sketchPlane" : qUnion([Q0])});
            skText(sketch, "E22", { "text": "Chiang Mai", "fontName": "OpenSans-Bold.ttf"});
            skText(sketch, "E23", { "text": "Maker Club", "fontName": "OpenSans-Bold.ttf"});
            const initialGuessF10  = {"E22": [-0.033, -0.0006, 1, 0, 0.0086], "E23": [-0.03, -0.018, 1, 0, 0.00755]};
            skSetInitialGuess(sketch, initialGuessF10);
            skSolve(sketch);
        }
        {
            var Q0;
            Q0 = qSketchRegion(id + "F10", true);
            extrude(context, id + "F11", {"entities" : qUnion([Q0]), "operationType" : NewBodyOperationType.REMOVE, "oppositeDirection" : true, "depth" : 1 * mm, "offsetDistance" : 25 * mm});
        }
        {
            var Q0;
            {var subQ0=sQuery(id+"F0.wireOp",EDGE,"E0.right");var subQ1=sQuery(id+"F0.wireOp",EDGE,"E0.left");var subQ2=sQuery(id+"F0.wireOp",EDGE,"E0.top");var subQ3=sQuery(id+"F0.wireOp",EDGE,"E0.bottom");Q0=makeQuery(id+"F11.boolean.opBoolean","SPLIT",FACE,{"disambiguationData":[TD([makeQuery(id+"F1.opExtrude","SWEPT_FACE",FACE,{"disambiguationData":[OSD([subQ3])]})])],"derivedFrom":makeQuery(id+"F2.opExtrude","CAP_FACE",FACE,{"disambiguationData":[OSD([subQ3,subQ2,subQ1,subQ0])],"isStart":false})});}
            var sketch = newSketch(context, id + "F12", { "sketchPlane" : qUnion([Q0])});
            skLineSegment(sketch, "E24", {"start": v(-6.59, 21.1) * mm, "end": v(-6.59, 22.56) * mm});
            skLineSegment(sketch, "E25", {"start": v(-6.59, 22.56) * mm, "end": v(-4.62, 24.4) * mm});
            skLineSegment(sketch, "E26", {"start": v(-4.62, 24.4) * mm, "end": v(-2.03, 21.88) * mm});
            skLineSegment(sketch, "E27", {"start": v(-2.03, 21.88) * mm, "end": v(0.63, 24.4) * mm});
            skLineSegment(sketch, "E28", {"start": v(0.63, 24.4) * mm, "end": v(2.5, 22.63) * mm});
            skLineSegment(sketch, "E29", {"start": v(2.5, 22.63) * mm, "end": v(2.5, 21.06) * mm});
            skLineSegment(sketch, "E30", {"start": v(2.5, 21.06) * mm, "end": v(3.04, 21.06) * mm});
            skLineSegment(sketch, "E31", {"start": v(3.04, 21.06) * mm, "end": v(3.04, 22.96) * mm});
            skLineSegment(sketch, "E32", {"start": v(3.04, 22.96) * mm, "end": v(1.01, 24.9) * mm});
            skLineSegment(sketch, "E33", {"start": v(1.01, 24.9) * mm, "end": v(0.27, 24.9) * mm});
            skLineSegment(sketch, "E34", {"start": v(0.27, 24.9) * mm, "end": v(-1.96, 22.77) * mm});
            skLineSegment(sketch, "E35", {"start": v(-1.96, 22.77) * mm, "end": v(-4.3, 24.94) * mm});
            skLineSegment(sketch, "E36", {"start": v(-4.3, 24.94) * mm, "end": v(-5.03, 24.94) * mm});
            skLineSegment(sketch, "E37", {"start": v(-5.03, 24.94) * mm, "end": v(-7.17, 22.88) * mm});
            skLineSegment(sketch, "E38", {"start": v(-7.17, 22.88) * mm, "end": v(-7.17, 21.07) * mm});
            skLineSegment(sketch, "E39", {"start": v(-7.17, 21.07) * mm, "end": v(-6.59, 21.1) * mm});
            skLineSegment(sketch, "E40", {"start": v(-5.53, 24.74) * mm, "end": v(-4.98, 25.14) * mm});
            skFitSpline(sketch, "E41", {"points": [v(-4.98, 25.14) * mm, v(-4.88, 26.3) * mm, v(-4.52, 27.65) * mm, v(-3.66, 28.56) * mm, v(-2.66, 29.01) * mm, v(-1.23, 28.98) * mm, v(-0.11, 28.48) * mm, v(0.57, 27.63) * mm, v(0.93, 26.69) * mm, v(1.06, 25.9) * mm, v(1.07, 25.14) * mm], "startDerivative": vector(0.71, 11.03) * mm, "endDerivative": vector(-0.07, -9.21) * mm});
            skLineSegment(sketch, "E42", {"start": v(1.07, 25.14) * mm, "end": v(1.7, 24.62) * mm});
            skFitSpline(sketch, "E43", {"points": [v(1.7, 24.62) * mm, v(1.7, 25.54) * mm, v(1.5, 26.82) * mm, v(1, 28.05) * mm, v(0.2, 28.9) * mm, v(-0.9, 29.43) * mm, v(-2.04, 29.57) * mm, v(-3.08, 29.44) * mm, v(-3.98, 29.02) * mm, v(-4.64, 28.5) * mm, v(-5.21, 27.52) * mm, v(-5.5, 26.34) * mm, v(-5.58, 25.32) * mm, v(-5.53, 24.74) * mm], "startDerivative": vector(0.4, 12.35) * mm, "endDerivative": vector(2.9, -8.52) * mm});
            skLineSegment(sketch, "E44", {"start": v(-2.36, 29.56) * mm, "end": v(-2.36, 30.75) * mm});
            skLineSegment(sketch, "E45", {"start": v(-2.36, 30.75) * mm, "end": v(-2.07, 31.06) * mm});
            skLineSegment(sketch, "E46", {"start": v(-2.07, 31.06) * mm, "end": v(-1.74, 30.75) * mm});
            skLineSegment(sketch, "E47", {"start": v(-1.74, 30.75) * mm, "end": v(-1.74, 29.56) * mm});
            skLineSegment(sketch, "E48", {"start": v(0.94, 23.74) * mm, "end": v(1.42, 23.26) * mm});
            skFitSpline(sketch, "E49", {"points": [v(1.42, 23.26) * mm, v(1.36, 22.7) * mm, v(1.18, 21.88) * mm, v(0.88, 21.02) * mm, v(0.6, 20.4) * mm], "startDerivative": vector(-0.19, -2.45) * mm, "endDerivative": vector(-1.2, -2.47) * mm});
            skFitSpline(sketch, "E50", {"points": [v(0.94, 23.74) * mm, v(0.85, 23.13) * mm, v(0.68, 22.42) * mm, v(0.41, 21.59) * mm, v(0.1, 20.86) * mm, v(-0.18, 20.33) * mm, v(-0.38, 19.99) * mm, v(-0.62, 19.66) * mm, v(-0.95, 19.27) * mm, v(-1.27, 19.02) * mm, v(-1.46, 18.88) * mm, v(-2.26, 18.85) * mm, v(-2.8, 19.13) * mm, v(-3.08, 19.43) * mm, v(-3.6, 20.04) * mm, v(-3.86, 20.54) * mm, v(-4.12, 21.14) * mm, v(-4.31, 21.59) * mm, v(-4.48, 22.05) * mm, v(-4.6, 22.43) * mm, v(-4.73, 23.01) * mm, v(-4.8, 23.43) * mm, v(-4.9, 23.98) * mm], "startDerivative": vector(-1.52, -12.5) * mm, "endDerivative": vector(-2.96, 12.5) * mm});
            skLineSegment(sketch, "E51", {"start": v(-4.86, 23.79) * mm, "end": v(-5.43, 23.36) * mm});
            skFitSpline(sketch, "E52", {"points": [v(-5.43, 23.36) * mm, v(-5.36, 22.95) * mm, v(-5.25, 22.51) * mm, v(-5.14, 22.1) * mm, v(-5, 21.65) * mm, v(-4.9, 21.31) * mm, v(-4.78, 21.01) * mm, v(-4.65, 20.63) * mm, v(-4.51, 20.4) * mm, v(-4.5, 20.4) * mm], "startDerivative": vector(0.43, -3.16) * mm, "endDerivative": vector(0.3, 0.61) * mm});
            skLineSegment(sketch, "E53", {"start": v(-4.5, 20.4) * mm, "end": v(-6.33, 20.4) * mm});
            skLineSegment(sketch, "E54", {"start": v(-6.33, 20.4) * mm, "end": v(-6.6, 20.64) * mm});
            skLineSegment(sketch, "E55", {"start": v(-6.6, 20.64) * mm, "end": v(-7.12, 20.64) * mm});
            skLineSegment(sketch, "E56", {"start": v(-7.12, 20.64) * mm, "end": v(-7.12, 20.15) * mm});
            skFitSpline(sketch, "E57", {"points": [v(-7.12, 20.15) * mm, v(-6.85, 19.87) * mm, v(-6.53, 19.75) * mm], "startDerivative": vector(0.48, -0.63) * mm, "endDerivative": vector(0.71, -0.17) * mm});
            skLineSegment(sketch, "E58", {"start": v(-6.53, 19.75) * mm, "end": v(-4.15, 19.75) * mm});
            skFitSpline(sketch, "E59", {"points": [v(-4.15, 19.75) * mm, v(-3.98, 19.43) * mm, v(-3.78, 19.16) * mm, v(-3.48, 18.86) * mm, v(-3.18, 18.6) * mm, v(-3.08, 18.54) * mm], "startDerivative": vector(0.75, -1.56) * mm, "endDerivative": vector(0.67, -0.45) * mm});
            skFitSpline(sketch, "E60", {"points": [v(-3.08, 18.54) * mm, v(-3.38, 18.25) * mm, v(-3.55, 18.01) * mm, v(-3.8, 17.52) * mm, v(-3.9, 17.15) * mm, v(-3.97, 16.68) * mm, v(-3.97, 16.04) * mm], "startDerivative": vector(-2.14, -1.67) * mm, "endDerivative": vector(0.17, -3.34) * mm});
            skLineSegment(sketch, "E61", {"start": v(-3.97, 16.04) * mm, "end": v(0.12, 16.04) * mm});
            skFitSpline(sketch, "E62", {"points": [v(0.12, 16.04) * mm, v(0.12, 16.33) * mm, v(0.12, 16.7) * mm, v(0, 17.17) * mm, v(-0.13, 17.57) * mm, v(-0.29, 17.91) * mm, v(-0.52, 18.26) * mm, v(-0.95, 18.54) * mm], "startDerivative": vector(-0.05, 2.34) * mm, "endDerivative": vector(-2.92, 1.58) * mm});
            skFitSpline(sketch, "E63", {"points": [v(-0.95, 18.54) * mm, v(-0.73, 18.7) * mm, v(-0.52, 18.91) * mm, v(-0.32, 19.09) * mm, v(-0.14, 19.3) * mm, v(0.03, 19.55) * mm, v(0.11, 19.7) * mm], "startDerivative": vector(1.32, 0.78) * mm, "endDerivative": vector(0.26, 1.2) * mm});
            skLineSegment(sketch, "E64", {"start": v(0.11, 19.7) * mm, "end": v(2.53, 19.7) * mm});
            skFitSpline(sketch, "E65", {"points": [v(2.53, 19.7) * mm, v(2.72, 19.8) * mm, v(2.92, 20) * mm, v(3, 20.2) * mm], "startDerivative": vector(0.6, 0.25) * mm, "endDerivative": vector(0.18, 0.6) * mm});
            skLineSegment(sketch, "E66", {"start": v(3, 20.2) * mm, "end": v(3, 20.6) * mm});
            skLineSegment(sketch, "E67", {"start": v(3, 20.6) * mm, "end": v(2.51, 20.6) * mm});
            skLineSegment(sketch, "E68", {"start": v(2.51, 20.6) * mm, "end": v(2.35, 20.34) * mm});
            skLineSegment(sketch, "E69", {"start": v(2.35, 20.34) * mm, "end": v(0.6, 20.4) * mm});
            skLineSegment(sketch, "E70", {"start": v(-3.4, 16.65) * mm, "end": v(-0.55, 16.65) * mm});
            skFitSpline(sketch, "E71", {"points": [v(-0.55, 16.65) * mm, v(-0.55, 16.98) * mm, v(-0.63, 17.36) * mm, v(-0.84, 17.71) * mm, v(-1.2, 18.04) * mm, v(-1.57, 18.17) * mm, v(-2.25, 18.2) * mm, v(-2.85, 18.02) * mm, v(-3.17, 17.68) * mm, v(-3.33, 17.28) * mm, v(-3.4, 16.91) * mm, v(-3.4, 16.65) * mm], "startDerivative": vector(0.77, 9.9) * mm, "endDerivative": vector(-1.05, -3.91) * mm});
            skSolve(sketch);
        }
        {
            var Q0;
            Q0 = qSketchRegion(id + "F12", true);
            extrude(context, id + "F13", {"entities" : qUnion([Q0]), "oppositeDirection" : true, "depth" : 1 * mm, "offsetDistance" : 25 * mm});
        }
        {
            var Q0;
            Q0=makeQuery(id+"F13.opExtrude","SWEPT_BODY",BODY,{"disambiguationData":[OSD([sQuery(id+"F12.wireOp",EDGE,"E24"),sQuery(id+"F12.wireOp",EDGE,"E25"),sQuery(id+"F12.wireOp",EDGE,"E26"),sQuery(id+"F12.wireOp",EDGE,"E27"),sQuery(id+"F12.wireOp",EDGE,"E28"),sQuery(id+"F12.wireOp",EDGE,"E29"),sQuery(id+"F12.wireOp",EDGE,"E30"),sQuery(id+"F12.wireOp",EDGE,"E31"),sQuery(id+"F12.wireOp",EDGE,"E32"),sQuery(id+"F12.wireOp",EDGE,"E33"),sQuery(id+"F12.wireOp",EDGE,"E34"),sQuery(id+"F12.wireOp",EDGE,"E35"),sQuery(id+"F12.wireOp",EDGE,"E36"),sQuery(id+"F12.wireOp",EDGE,"E37"),sQuery(id+"F12.wireOp",EDGE,"E38"),sQuery(id+"F12.wireOp",EDGE,"E39")])]});
            var Q1;
            Q1=makeQuery(id+"F13.opExtrude","SWEPT_BODY",BODY,{"disambiguationData":[OSD([sQuery(id+"F12.wireOp",EDGE,"E40"),sQuery(id+"F12.wireOp",EDGE,"E41"),sQuery(id+"F12.wireOp",EDGE,"E42"),sQuery(id+"F12.wireOp",EDGE,"E43"),sQuery(id+"F12.wireOp",EDGE,"E44"),sQuery(id+"F12.wireOp",EDGE,"E45"),sQuery(id+"F12.wireOp",EDGE,"E46"),sQuery(id+"F12.wireOp",EDGE,"E47")])]});
            var Q2;
            Q2=makeQuery(id+"F13.opExtrude","SWEPT_BODY",BODY,{"disambiguationData":[OSD([sQuery(id+"F12.wireOp",EDGE,"E48"),sQuery(id+"F12.wireOp",EDGE,"E49"),sQuery(id+"F12.wireOp",EDGE,"E50"),sQuery(id+"F12.wireOp",EDGE,"E51"),sQuery(id+"F12.wireOp",EDGE,"E52"),sQuery(id+"F12.wireOp",EDGE,"E53"),sQuery(id+"F12.wireOp",EDGE,"E54"),sQuery(id+"F12.wireOp",EDGE,"E55"),sQuery(id+"F12.wireOp",EDGE,"E56"),sQuery(id+"F12.wireOp",EDGE,"E57"),sQuery(id+"F12.wireOp",EDGE,"E58"),sQuery(id+"F12.wireOp",EDGE,"E59"),sQuery(id+"F12.wireOp",EDGE,"E60"),sQuery(id+"F12.wireOp",EDGE,"E61"),sQuery(id+"F12.wireOp",EDGE,"E62"),sQuery(id+"F12.wireOp",EDGE,"E63"),sQuery(id+"F12.wireOp",EDGE,"E64"),sQuery(id+"F12.wireOp",EDGE,"E65"),sQuery(id+"F12.wireOp",EDGE,"E66"),sQuery(id+"F12.wireOp",EDGE,"E67"),sQuery(id+"F12.wireOp",EDGE,"E68"),sQuery(id+"F12.wireOp",EDGE,"E69"),sQuery(id+"F12.wireOp",EDGE,"E70"),sQuery(id+"F12.wireOp",EDGE,"E71")])]});
            transform(context, id + "F14", {"entities" : qUnion([Q0, Q1, Q2]), "transformType" : TransformType.TRANSLATION_3D, "dx" : 2 * mm, "dy" : 0 * mm, "dz" : 0 * mm, "makeCopy" : false});
        }
        {
            var Q0;
            Q0=makeQuery(id+"F13.opExtrude","SWEPT_BODY",BODY,{"disambiguationData":[OSD([sQuery(id+"F12.wireOp",EDGE,"E24"),sQuery(id+"F12.wireOp",EDGE,"E25"),sQuery(id+"F12.wireOp",EDGE,"E26"),sQuery(id+"F12.wireOp",EDGE,"E27"),sQuery(id+"F12.wireOp",EDGE,"E28"),sQuery(id+"F12.wireOp",EDGE,"E29"),sQuery(id+"F12.wireOp",EDGE,"E30"),sQuery(id+"F12.wireOp",EDGE,"E31"),sQuery(id+"F12.wireOp",EDGE,"E32"),sQuery(id+"F12.wireOp",EDGE,"E33"),sQuery(id+"F12.wireOp",EDGE,"E34"),sQuery(id+"F12.wireOp",EDGE,"E35"),sQuery(id+"F12.wireOp",EDGE,"E36"),sQuery(id+"F12.wireOp",EDGE,"E37"),sQuery(id+"F12.wireOp",EDGE,"E38"),sQuery(id+"F12.wireOp",EDGE,"E39")])]});
            var Q1;
            Q1=makeQuery(id+"F13.opExtrude","SWEPT_BODY",BODY,{"disambiguationData":[OSD([sQuery(id+"F12.wireOp",EDGE,"E40"),sQuery(id+"F12.wireOp",EDGE,"E41"),sQuery(id+"F12.wireOp",EDGE,"E42"),sQuery(id+"F12.wireOp",EDGE,"E43"),sQuery(id+"F12.wireOp",EDGE,"E44"),sQuery(id+"F12.wireOp",EDGE,"E45"),sQuery(id+"F12.wireOp",EDGE,"E46"),sQuery(id+"F12.wireOp",EDGE,"E47")])]});
            var Q2;
            Q2=makeQuery(id+"F13.opExtrude","SWEPT_BODY",BODY,{"disambiguationData":[OSD([sQuery(id+"F12.wireOp",EDGE,"E48"),sQuery(id+"F12.wireOp",EDGE,"E49"),sQuery(id+"F12.wireOp",EDGE,"E50"),sQuery(id+"F12.wireOp",EDGE,"E51"),sQuery(id+"F12.wireOp",EDGE,"E52"),sQuery(id+"F12.wireOp",EDGE,"E53"),sQuery(id+"F12.wireOp",EDGE,"E54"),sQuery(id+"F12.wireOp",EDGE,"E55"),sQuery(id+"F12.wireOp",EDGE,"E56"),sQuery(id+"F12.wireOp",EDGE,"E57"),sQuery(id+"F12.wireOp",EDGE,"E58"),sQuery(id+"F12.wireOp",EDGE,"E59"),sQuery(id+"F12.wireOp",EDGE,"E60"),sQuery(id+"F12.wireOp",EDGE,"E61"),sQuery(id+"F12.wireOp",EDGE,"E62"),sQuery(id+"F12.wireOp",EDGE,"E63"),sQuery(id+"F12.wireOp",EDGE,"E64"),sQuery(id+"F12.wireOp",EDGE,"E65"),sQuery(id+"F12.wireOp",EDGE,"E66"),sQuery(id+"F12.wireOp",EDGE,"E67"),sQuery(id+"F12.wireOp",EDGE,"E68"),sQuery(id+"F12.wireOp",EDGE,"E69"),sQuery(id+"F12.wireOp",EDGE,"E70"),sQuery(id+"F12.wireOp",EDGE,"E71")])]});
            var Q3;
            Q3=makeQuery(id+"F1.opExtrude","SWEPT_BODY",BODY,{"disambiguationData":[OSD([sQuery(id+"F0.wireOp",EDGE,"E0.bottom"),sQuery(id+"F0.wireOp",EDGE,"E0.top"),sQuery(id+"F0.wireOp",EDGE,"E0.left"),sQuery(id+"F0.wireOp",EDGE,"E0.right"),sQuery(id+"F0.wireOp",EDGE,"E1.0"),sQuery(id+"F0.wireOp",EDGE,"E1.1"),sQuery(id+"F0.wireOp",EDGE,"E1.2"),sQuery(id+"F0.wireOp",EDGE,"E1.3")])]});
            booleanBodies(context, id + "F15", {"operationType" : BooleanOperationType.SUBTRACTION, "tools" : qUnion([Q0, Q1, Q2]), "targets" : qUnion([Q3])});
        }
        {
            var Q0;
            Q0=makeQuery(id+"F2.opExtrude","CAP_EDGE",EDGE,{"disambiguationData":[OSD([sQuery(id+"F0.wireOp",EDGE,"E0.bottom")])],"isStart":false});
            fillet(context, id + "F16", {"entities" : qUnion([Q0]), "radius" : 1 * mm, "tangentPropagation" : true, "allowEdgeOverflow" : false});
        }
    });